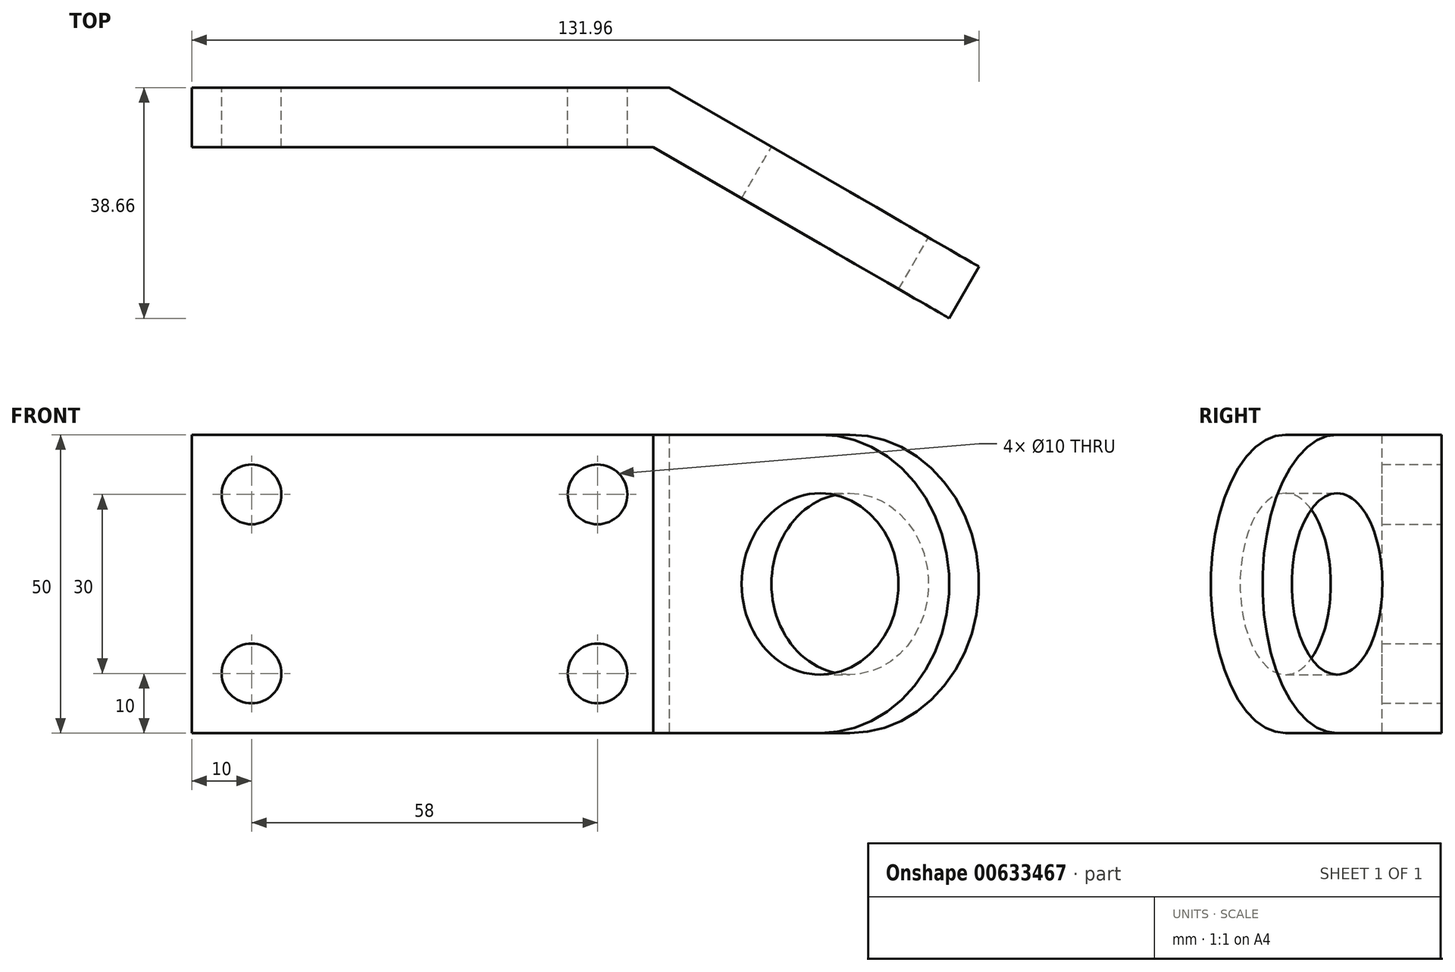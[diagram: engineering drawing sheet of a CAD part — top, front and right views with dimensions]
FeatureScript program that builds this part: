
annotation { "Feature Type Name" : "Feature", "Feature Type Description" : "" }
export const myFeature = defineFeature(function(context is Context, id is Id, definition is map)
    precondition{}
    {
        {
            var Q0;
            Q0=qCreatedBy(makeId("Top.planeOp"),FACE);
            var sketch = newSketch(context, id + "F0", { "sketchPlane" : qUnion([Q0])});
            skLineSegment(sketch, "E0", {"start": v(-80, 29.68) * mm, "end": v(0, 29.68) * mm});
            skLineSegment(sketch, "E1", {"start": v(0, 29.68) * mm, "end": v(51.96, -0.32) * mm});
            skLineSegment(sketch, "E2.0", {"start": v(-2.68, 19.68) * mm, "end": v(46.96, -8.98) * mm});
            skLineSegment(sketch, "E2.1", {"start": v(-80, 19.68) * mm, "end": v(-2.68, 19.68) * mm});
            skLineSegment(sketch, "E3", {"start": v(-80, 29.68) * mm, "end": v(-80, 19.68) * mm});
            skLineSegment(sketch, "E4", {"start": v(51.96, -0.32) * mm, "end": v(46.96, -8.98) * mm});
            skSolve(sketch);
        }
        {
            var Q0;
            Q0 = qSketchRegion(id + "F0", true);
            extrude(context, id + "F1", {"entities" : qUnion([Q0]), "depth" : 50 * mm, "offsetDistance" : 25 * mm});
        }
        {
            var Q0;
            Q0=makeQuery(id+"F1.opExtrude","CAP_EDGE",EDGE,{"disambiguationData":[OSD([sQuery(id+"F0.wireOp",EDGE,"E4")])],"isStart":false});
            var Q1;
            Q1=makeQuery(id+"F1.opExtrude","CAP_EDGE",EDGE,{"disambiguationData":[OSD([sQuery(id+"F0.wireOp",EDGE,"E4")])],"isStart":true});
            fillet(context, id + "F2", {"entities" : qUnion([Q0, Q1]), "radius" : 25 * mm, "tangentPropagation" : true, "allowEdgeOverflow" : false});
        }
        {
            var Q0;
            Q0=makeQuery(id+"F1.opExtrude","SWEPT_FACE",FACE,{"disambiguationData":[OSD([sQuery(id+"F0.wireOp",EDGE,"E1")])]});
            var sketch = newSketch(context, id + "F3", { "sketchPlane" : qUnion([Q0])});
            skCircle(sketch, "E5", {"center": v(-20.16, 25) * mm, "radius": 15.2 * mm});
            skSolve(sketch);
        }
        {
            var Q0;
            Q0 = qSketchRegion(id + "F3", true);
            extrude(context, id + "F4", {"entities" : qUnion([Q0]), "operationType" : NewBodyOperationType.REMOVE, "endBound" : BoundingType.THROUGH_ALL, "oppositeDirection" : true, "depth" : 25 * mm, "offsetDistance" : 25 * mm});
        }
        {
            var Q0;
            Q0=makeQuery(id+"F1.opExtrude","SWEPT_FACE",FACE,{"disambiguationData":[OSD([sQuery(id+"F0.wireOp",EDGE,"E0")])]});
            var sketch = newSketch(context, id + "F5", { "sketchPlane" : qUnion([Q0])});
            skCircle(sketch, "E6", {"center": v(70, 40) * mm, "radius": 5 * mm});
            skCircle(sketch, "E7.0.1.0", {"center": v(70, 10) * mm, "radius": 5 * mm});
            skCircle(sketch, "E7.1.0.0", {"center": v(12, 40) * mm, "radius": 5 * mm});
            skCircle(sketch, "E7.1.1.0", {"center": v(12, 10) * mm, "radius": 5 * mm});
            skLineSegment(sketch, "E7.direction1", {"start": v(70, 40) * mm, "end": v(12, 40) * mm, "construction": true});
            skLineSegment(sketch, "E7.direction2", {"start": v(70, 40) * mm, "end": v(70, 10) * mm, "construction": true});
            skSolve(sketch);
        }
        {
            var Q0;
            Q0=makeQuery(id+"F5.imprint","IMPRINT",FACE,{"disambiguationData":[TD([[makeQuery(id+"F5.imprint","IMPRINT",EDGE,{"derivedFrom":sQuery(id+"F5.wireOp",EDGE,"E7.1.0.0")}),1.0]])]});
            var Q1;
            Q1=makeQuery(id+"F5.imprint","IMPRINT",FACE,{"disambiguationData":[TD([[makeQuery(id+"F5.imprint","IMPRINT",EDGE,{"derivedFrom":sQuery(id+"F5.wireOp",EDGE,"E6")}),1.0]])]});
            var Q2;
            Q2=makeQuery(id+"F5.imprint","IMPRINT",FACE,{"disambiguationData":[TD([[makeQuery(id+"F5.imprint","IMPRINT",EDGE,{"derivedFrom":sQuery(id+"F5.wireOp",EDGE,"E7.1.1.0")}),1.0]])]});
            var Q3;
            Q3=makeQuery(id+"F5.imprint","IMPRINT",FACE,{"disambiguationData":[TD([[makeQuery(id+"F5.imprint","IMPRINT",EDGE,{"derivedFrom":sQuery(id+"F5.wireOp",EDGE,"E7.0.1.0")}),1.0]])]});
            extrude(context, id + "F6", {"entities" : qUnion([Q0, Q1, Q2, Q3]), "operationType" : NewBodyOperationType.REMOVE, "endBound" : BoundingType.THROUGH_ALL, "oppositeDirection" : true, "depth" : 25 * mm, "offsetDistance" : 25 * mm});
        }
    });
